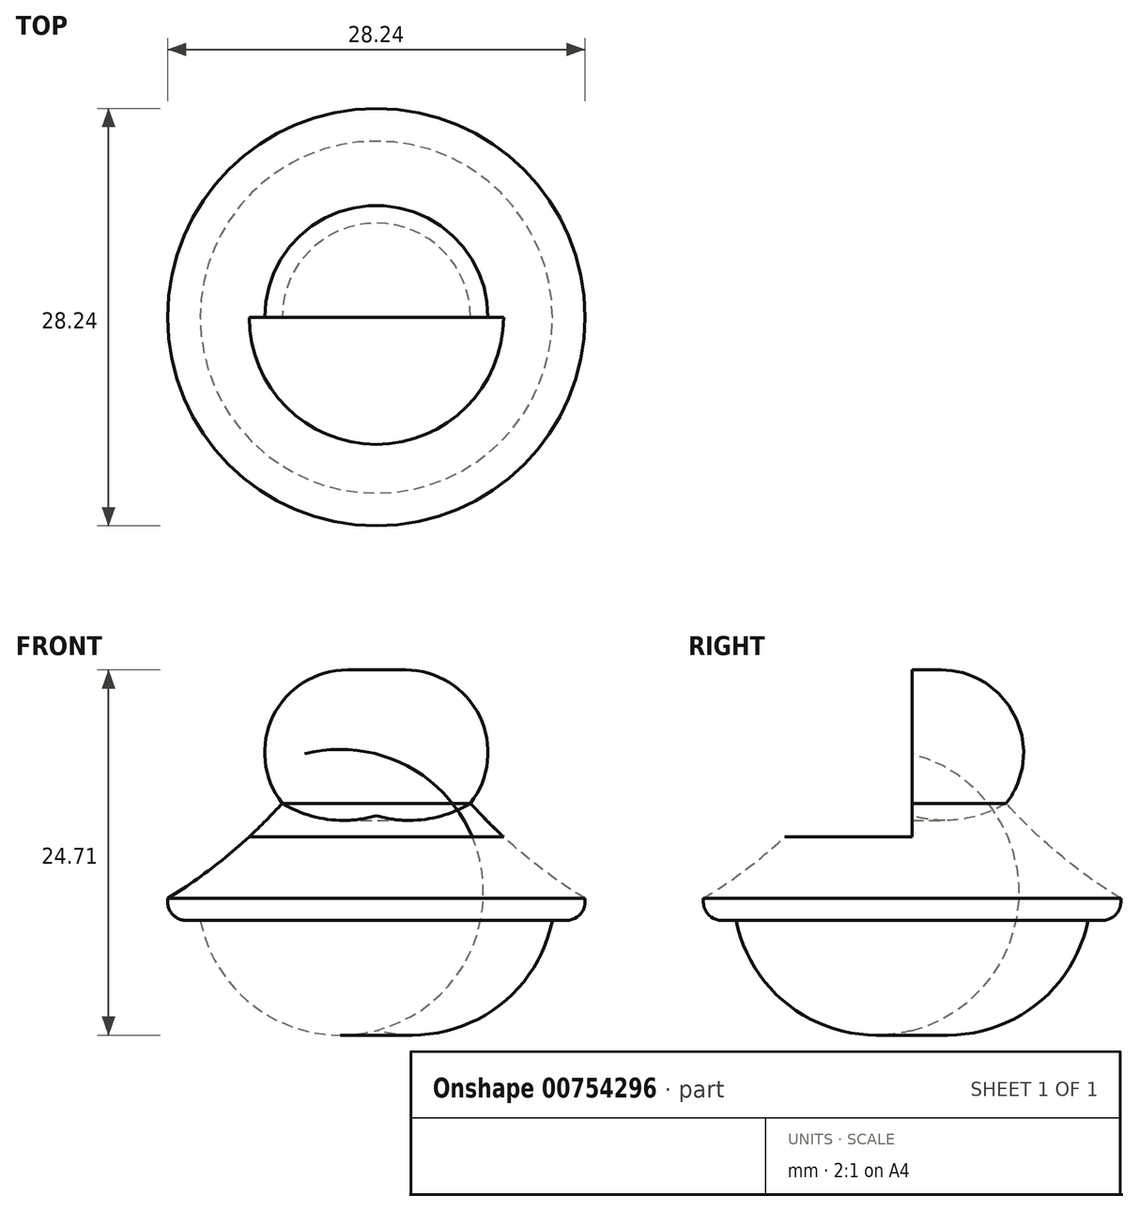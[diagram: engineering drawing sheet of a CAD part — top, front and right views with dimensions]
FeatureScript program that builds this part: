
annotation { "Feature Type Name" : "Feature", "Feature Type Description" : "" }
export const myFeature = defineFeature(function(context is Context, id is Id, definition is map)
    precondition{}
    {
        {
            var Q0;
            Q0=qCreatedBy(makeId("Front.planeOp"),FACE);
            var sketch = newSketch(context, id + "F0", { "sketchPlane" : qUnion([Q0])});
            skLineSegment(sketch, "E0", {"start": v(0, 0) * mm, "end": v(0, 68.69) * mm});
            skArc(sketch, "E1", {"start": v(-11.9, 7.45) * mm, "mid": v(-7.56, 1.16) * mm, "end": v(0, 0) * mm});
            skLineSegment(sketch, "E2", {"start": v(-11.9, 7.45) * mm, "end": v(0, 7.45) * mm});
            skLineSegment(sketch, "E3", {"start": v(-11.9, 7.45) * mm, "end": v(-14.12, 7.45) * mm});
            skLineSegment(sketch, "E4", {"start": v(-14.12, 7.45) * mm, "end": v(-14.12, 8.94) * mm});
            skArc(sketch, "E5", {"start": v(-6.37, 15.38) * mm, "mid": v(-3.27, 14.3) * mm, "end": v(0, 14.53) * mm});
            skArc(sketch, "E6", {"start": v(-14.12, 8.94) * mm, "mid": v(-10.01, 11.88) * mm, "end": v(-6.37, 15.38) * mm});
            skPoint(sketch, "E7.start.orphan", {"position": v(0, 22.76) * mm});
            skSolve(sketch);
        }
        {
            var Q0;
            {var subQ0=sQuery(id+"F0.wireOp",EDGE,"E1");Q0=makeQuery(id+"F0.imprint","IMPRINT",FACE,{"disambiguationData":[TD([[makeQuery(id+"F0.imprint","IMPRINT",EDGE,{"derivedFrom":subQ0}),1.0]])]});}
            var Q1;
            {var subQ0=sQuery(id+"F0.wireOp",EDGE,"E2");Q1=makeQuery(id+"F0.imprint","IMPRINT",FACE,{"disambiguationData":[TD([[makeQuery(id+"F0.imprint","IMPRINT",EDGE,{"derivedFrom":subQ0}),1.0]])]});}
            var Q2;
            {var subQ0=sQuery(id+"F0.wireOp",EDGE,"E5");Q2=makeQuery(id+"F0.imprint","IMPRINT",FACE,{"disambiguationData":[TD([[makeQuery(id+"F0.imprint","IMPRINT",EDGE,{"derivedFrom":subQ0}),1.0]])]});}
            var Q3;
            Q3=sQuery(id+"F0.wireOp",EDGE,"E0");
            revolve(context, id + "F1", {"surfaceOperationType" : NewSurfaceOperationType.NEW, "entities" : qUnion([Q0, Q1, Q2]), "axis" : qUnion([Q3]), "revolveType" : RevolveType.FULL});
        }
        {
            var Q0;
            Q0=makeQuery(id+"F1.opRevolve","SWEPT_EDGE",EDGE,{"disambiguationData":[OSD([sQuery(id+"F0.wireOp",EDGE,"E3"),sQuery(id+"F0.wireOp",EDGE,"E4")])]});
            fillet(context, id + "F2", {"entities" : qUnion([Q0]), "radius" : 1.27 * mm, "tangentPropagation" : true, "allowEdgeOverflow" : false});
        }
        {
            var Q0;
            Q0=qCreatedBy(makeId("Front.planeOp"),FACE);
            var sketch = newSketch(context, id + "F3", { "sketchPlane" : qUnion([Q0])});
            skLineSegment(sketch, "E8.0", {"start": v(6.37, 15.38) * mm, "end": v(-6.37, 15.38) * mm});
            skLineSegment(sketch, "E9", {"start": v(0, 15.38) * mm, "end": v(0, 30.38) * mm});
            skLineSegment(sketch, "E10", {"start": v(0, 24.4) * mm, "end": v(-1.97, 24.4) * mm});
            skArc(sketch, "E11", {"start": v(-1.97, 24.4) * mm, "mid": v(-6.99, 21.26) * mm, "end": v(-6.37, 15.38) * mm});
            skSolve(sketch);
        }
        {
            var Q0;
            {var subQ4=sQuery(id+"F3.wireOp",EDGE,"E10");Q0=makeQuery(id+"F3.imprint","IMPRINT",FACE,{"disambiguationData":[TD([[makeQuery(id+"F3.imprint","IMPRINT",EDGE,{"derivedFrom":subQ4}),1.0]])]});}
            var Q1;
            Q1=sQuery(id+"F3.wireOp",EDGE,"E9");
            revolve(context, id + "F4", {"surfaceOperationType" : NewSurfaceOperationType.NEW, "entities" : qUnion([Q0]), "axis" : qUnion([Q1]), "revolveType" : RevolveType.FULL});
        }
        {
            var Q0;
            Q0=qCreatedBy(makeId("Front.planeOp"),FACE);
            var sketch = newSketch(context, id + "F5", { "sketchPlane" : qUnion([Q0])});
            skLineSegment(sketch, "E12.bottom", {"start": v(-12.58, 28.94) * mm, "end": v(15.47, 28.94) * mm});
            skLineSegment(sketch, "E12.top", {"start": v(-12.58, 13.1) * mm, "end": v(15.47, 13.1) * mm});
            skLineSegment(sketch, "E12.left", {"start": v(-12.58, 28.94) * mm, "end": v(-12.58, 13.1) * mm});
            skLineSegment(sketch, "E12.right", {"start": v(15.47, 28.94) * mm, "end": v(15.47, 13.1) * mm});
            skSolve(sketch);
        }
        {
            var Q0;
            Q0 = qSketchRegion(id + "F5", true);
            extrude(context, id + "F6", {"entities" : qUnion([Q0]), "operationType" : NewBodyOperationType.REMOVE, "depth" : 25.4 * mm, "offsetDistance" : 25.4 * mm});
        }
    });
